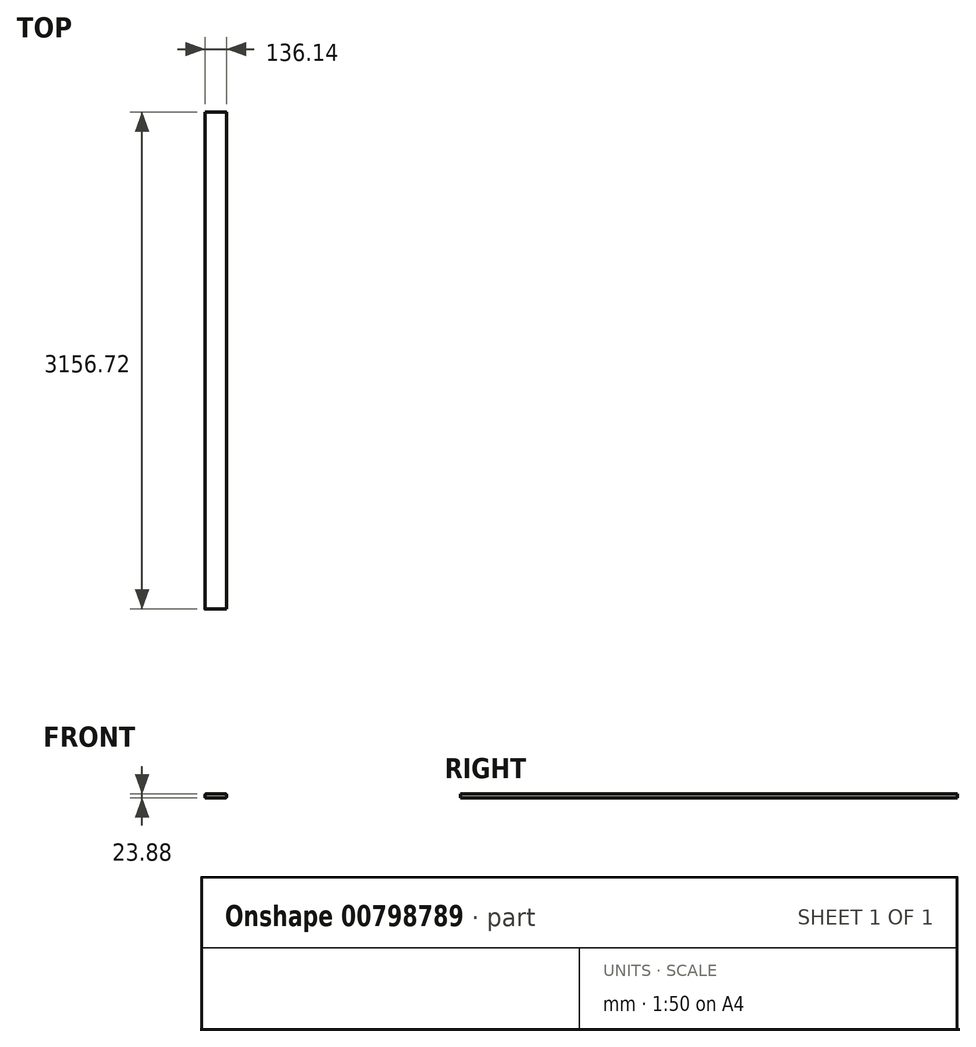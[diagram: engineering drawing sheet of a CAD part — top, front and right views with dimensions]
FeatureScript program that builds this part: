
annotation { "Feature Type Name" : "Feature", "Feature Type Description" : "" }
export const myFeature = defineFeature(function(context is Context, id is Id, definition is map)
    precondition{}
    {
        {
            var Q0;
            Q0=qCreatedBy(makeId("Front.planeOp"),FACE);
            var sketch = newSketch(context, id + "F0", { "sketchPlane" : qUnion([Q0])});
            skLineSegment(sketch, "E0.bottom", {"start": v(-63.25, 11.94) * mm, "end": v(63.25, 11.94) * mm});
            skLineSegment(sketch, "E0.top", {"start": v(-63.25, -11.94) * mm, "end": v(63.25, -11.94) * mm});
            skLineSegment(sketch, "E0.left", {"start": v(-68.07, 7.11) * mm, "end": v(-68.07, -7.11) * mm});
            skLineSegment(sketch, "E0.right", {"start": v(68.07, 7.11) * mm, "end": v(68.07, -7.11) * mm});
            skPoint(sketch, "E0.middle", {"position": v(0, 0) * mm});
            skPoint(sketch, "E1.visualSharp", {"position": v(-68.07, 11.94) * mm});
            skArc(sketch, "E1.filletArc", {"start": v(-63.25, 11.94) * mm, "mid": v(-66.66, 10.52) * mm, "end": v(-68.07, 7.11) * mm});
            skPoint(sketch, "E2.visualSharp", {"position": v(68.07, 11.94) * mm});
            skArc(sketch, "E2.filletArc", {"start": v(68.07, 7.11) * mm, "mid": v(66.66, 10.52) * mm, "end": v(63.25, 11.94) * mm});
            skPoint(sketch, "E3.visualSharp", {"position": v(68.07, -11.94) * mm});
            skArc(sketch, "E3.filletArc", {"start": v(63.25, -11.94) * mm, "mid": v(66.66, -10.52) * mm, "end": v(68.07, -7.11) * mm});
            skPoint(sketch, "E4.visualSharp", {"position": v(-68.07, -11.94) * mm});
            skArc(sketch, "E4.filletArc", {"start": v(-68.07, -7.11) * mm, "mid": v(-66.66, -10.52) * mm, "end": v(-63.25, -11.94) * mm});
            skSolve(sketch);
        }
        {
            var Q0;
            Q0=makeQuery(id+"F0.imprint","IMPRINT",FACE,{"disambiguationData":[TD([[makeQuery(id+"F0.imprint","IMPRINT",EDGE,{"derivedFrom":sQuery(id+"F0.wireOp",EDGE,"E0.bottom")}),-1.0]])]});
            extrude(context, id + "F1", {"entities" : qUnion([Q0]), "endBound" : BoundingType.SYMMETRIC, "depth" : 3156.71 * mm, "offsetDistance" : 25.4 * mm});
        }
    });
